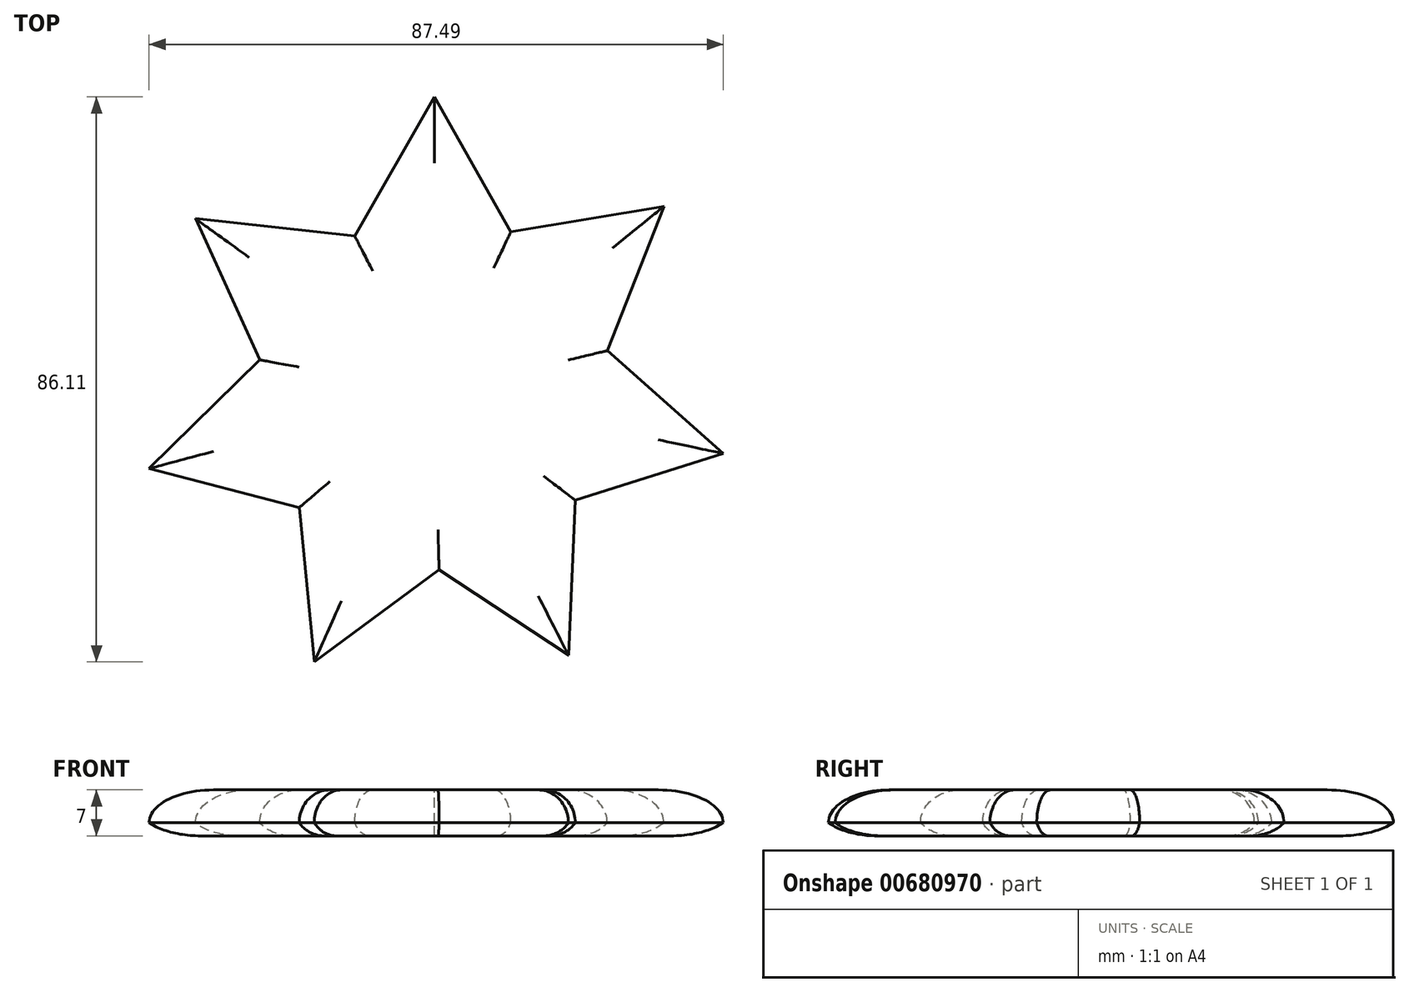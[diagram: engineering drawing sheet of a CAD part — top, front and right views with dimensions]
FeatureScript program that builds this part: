
annotation { "Feature Type Name" : "Feature", "Feature Type Description" : "" }
export const myFeature = defineFeature(function(context is Context, id is Id, definition is map)
    precondition{}
    {
        {
            var Q0;
            Q0=qCreatedBy(makeId("Top.planeOp"),FACE);
            var sketch = newSketch(context, id + "F0", { "sketchPlane" : qUnion([Q0])});
            skCircle(sketch, "E0", {"center": v(0, 0) * mm, "radius": 12.64 * mm});
            skCircle(sketch, "E1", {"center": v(0, 0) * mm, "radius": 17.03 * mm});
            skLineSegment(sketch, "E2", {"start": v(0, 0) * mm, "end": v(0, 45) * mm});
            skLineSegment(sketch, "E3", {"start": v(0, 0) * mm, "end": v(34.97, 28.32) * mm});
            skLineSegment(sketch, "E4", {"start": v(0, 0) * mm, "end": v(-18.3, -41.1) * mm});
            skLineSegment(sketch, "E5", {"start": v(0, 0) * mm, "end": v(-43.47, -11.65) * mm});
            skLineSegment(sketch, "E6", {"start": v(0, 0) * mm, "end": v(44.02, -9.36) * mm});
            skLineSegment(sketch, "E7", {"start": v(0, 0) * mm, "end": v(20.43, -40.1) * mm});
            skLineSegment(sketch, "E8", {"start": v(0, 0) * mm, "end": v(-36.4, 26.45) * mm});
            skLineSegment(sketch, "E9", {"start": v(0, 0) * mm, "end": v(-18.2, 13.23) * mm});
            skLineSegment(sketch, "E10", {"start": v(0, 0) * mm, "end": v(-21.73, -5.82) * mm});
            skLineSegment(sketch, "E11", {"start": v(0, 0) * mm, "end": v(-9.15, -20.55) * mm});
            skLineSegment(sketch, "E12", {"start": v(0, 0) * mm, "end": v(10.21, -20.05) * mm});
            skLineSegment(sketch, "E13", {"start": v(0, 0) * mm, "end": v(22, -4.68) * mm});
            skLineSegment(sketch, "E14", {"start": v(0, 0) * mm, "end": v(17.49, 14.16) * mm});
            skLineSegment(sketch, "E15", {"start": v(0, 0) * mm, "end": v(0, 22.5) * mm});
            skLineSegment(sketch, "E16", {"start": v(0, 22.5) * mm, "end": v(-18.2, 13.23) * mm});
            skLineSegment(sketch, "E17", {"start": v(-18.2, 13.23) * mm, "end": v(-21.73, -5.82) * mm});
            skLineSegment(sketch, "E18", {"start": v(-21.73, -5.82) * mm, "end": v(-9.15, -20.55) * mm});
            skLineSegment(sketch, "E19", {"start": v(-9.15, -20.55) * mm, "end": v(10.21, -20.05) * mm});
            skLineSegment(sketch, "E20", {"start": v(10.21, -20.05) * mm, "end": v(22, -4.68) * mm});
            skLineSegment(sketch, "E21", {"start": v(22, -4.68) * mm, "end": v(17.49, 14.16) * mm});
            skLineSegment(sketch, "E22", {"start": v(17.49, 14.16) * mm, "end": v(0, 22.5) * mm});
            skLineSegment(sketch, "E23", {"start": v(0, 45) * mm, "end": v(17.49, 14.16) * mm});
            skLineSegment(sketch, "E24", {"start": v(34.97, 28.32) * mm, "end": v(0, 22.5) * mm});
            skLineSegment(sketch, "E25", {"start": v(34.97, 28.32) * mm, "end": v(22, -4.68) * mm});
            skLineSegment(sketch, "E26", {"start": v(44.02, -9.36) * mm, "end": v(17.49, 14.16) * mm});
            skLineSegment(sketch, "E27", {"start": v(44.02, -9.36) * mm, "end": v(10.21, -20.05) * mm});
            skLineSegment(sketch, "E28", {"start": v(20.43, -40.1) * mm, "end": v(22, -4.68) * mm});
            skLineSegment(sketch, "E29", {"start": v(20.43, -40.1) * mm, "end": v(-9.15, -20.55) * mm});
            skLineSegment(sketch, "E30", {"start": v(-18.3, -41.1) * mm, "end": v(10.21, -20.05) * mm});
            skLineSegment(sketch, "E31", {"start": v(-18.3, -41.1) * mm, "end": v(-21.73, -5.82) * mm});
            skLineSegment(sketch, "E32", {"start": v(-43.47, -11.65) * mm, "end": v(-9.15, -20.55) * mm});
            skLineSegment(sketch, "E33", {"start": v(-43.47, -11.65) * mm, "end": v(-18.2, 13.23) * mm});
            skLineSegment(sketch, "E34", {"start": v(-36.4, 26.45) * mm, "end": v(-21.73, -5.82) * mm});
            skLineSegment(sketch, "E35", {"start": v(-36.4, 26.45) * mm, "end": v(0, 22.5) * mm});
            skLineSegment(sketch, "E36", {"start": v(0, 45) * mm, "end": v(-18.2, 13.23) * mm});
            skSolve(sketch);
        }
        {
            var Q0;
            {var subQ0=sQuery(id+"F0.wireOp",EDGE,"E7");Q0=makeQuery(id+"F0.imprint","IMPRINT",FACE,{"disambiguationData":[TD([[makeQuery(id+"F0.imprint","IMPRINT",EDGE,{"derivedFrom":subQ0}),-1.0]])]});}
            var Q1;
            {var subQ0=sQuery(id+"F0.wireOp",EDGE,"E4");Q1=makeQuery(id+"F0.imprint","IMPRINT",FACE,{"disambiguationData":[TD([[makeQuery(id+"F0.imprint","IMPRINT",EDGE,{"derivedFrom":subQ0}),-1.0]])]});}
            var Q2;
            {var subQ0=sQuery(id+"F0.wireOp",EDGE,"E5");Q2=makeQuery(id+"F0.imprint","IMPRINT",FACE,{"disambiguationData":[TD([[makeQuery(id+"F0.imprint","IMPRINT",EDGE,{"derivedFrom":subQ0}),1.0]])]});}
            var Q3;
            {var subQ0=sQuery(id+"F0.wireOp",EDGE,"E2");Q3=makeQuery(id+"F0.imprint","IMPRINT",FACE,{"disambiguationData":[TD([[makeQuery(id+"F0.imprint","IMPRINT",EDGE,{"derivedFrom":subQ0}),1.0]])]});}
            var Q4;
            {var subQ0=sQuery(id+"F0.wireOp",EDGE,"E5");Q4=makeQuery(id+"F0.imprint","IMPRINT",FACE,{"disambiguationData":[TD([[makeQuery(id+"F0.imprint","IMPRINT",EDGE,{"derivedFrom":subQ0}),-1.0]])]});}
            var Q5;
            {var subQ0=sQuery(id+"F0.wireOp",EDGE,"E7");Q5=makeQuery(id+"F0.imprint","IMPRINT",FACE,{"disambiguationData":[TD([[makeQuery(id+"F0.imprint","IMPRINT",EDGE,{"derivedFrom":subQ0}),1.0]])]});}
            var Q6;
            {var subQ0=sQuery(id+"F0.wireOp",EDGE,"E8");Q6=makeQuery(id+"F0.imprint","IMPRINT",FACE,{"disambiguationData":[TD([[makeQuery(id+"F0.imprint","IMPRINT",EDGE,{"derivedFrom":subQ0}),1.0]])]});}
            var Q7;
            {var subQ5=sQuery(id+"F0.wireOp",EDGE,"E19");Q7=makeQuery(id+"F0.imprint","IMPRINT",FACE,{"disambiguationData":[TD([[makeQuery(id+"F0.imprint","IMPRINT",EDGE,{"derivedFrom":subQ5}),1.0]])]});}
            var Q8;
            {var subQ0=sQuery(id+"F0.wireOp",EDGE,"E2");Q8=makeQuery(id+"F0.imprint","IMPRINT",FACE,{"disambiguationData":[TD([[makeQuery(id+"F0.imprint","IMPRINT",EDGE,{"derivedFrom":subQ0}),-1.0]])]});}
            var Q9;
            {var subQ0=sQuery(id+"F0.wireOp",EDGE,"E4");Q9=makeQuery(id+"F0.imprint","IMPRINT",FACE,{"disambiguationData":[TD([[makeQuery(id+"F0.imprint","IMPRINT",EDGE,{"derivedFrom":subQ0}),1.0]])]});}
            var Q10;
            {var subQ0=sQuery(id+"F0.wireOp",EDGE,"E16");Q10=makeQuery(id+"F0.imprint","IMPRINT",FACE,{"disambiguationData":[TD([[makeQuery(id+"F0.imprint","IMPRINT",EDGE,{"derivedFrom":subQ0}),-1.0]])]});}
            var Q11;
            {var subQ0=sQuery(id+"F0.wireOp",EDGE,"E11");var subQ1=sQuery(id+"F0.wireOp",EDGE,"E0");var subQ2=makeQuery(id+"F0.imprint","INTERSECT",VERTEX,{"derivedFrom":[subQ1,subQ0]});Q11=makeQuery(id+"F0.imprint","IMPRINT",FACE,{"disambiguationData":[TD([[makeQuery(id+"F0.imprint","IMPRINT",EDGE,{"disambiguationData":[TD([[subQ2,-1.0]])],"derivedFrom":subQ1}),-1.0]])]});}
            var Q12;
            {var subQ0=sQuery(id+"F0.wireOp",EDGE,"E3");Q12=makeQuery(id+"F0.imprint","IMPRINT",FACE,{"disambiguationData":[TD([[makeQuery(id+"F0.imprint","IMPRINT",EDGE,{"derivedFrom":subQ0}),-1.0]])]});}
            var Q13;
            {var subQ0=sQuery(id+"F0.wireOp",EDGE,"E3");Q13=makeQuery(id+"F0.imprint","IMPRINT",FACE,{"disambiguationData":[TD([[makeQuery(id+"F0.imprint","IMPRINT",EDGE,{"derivedFrom":subQ0}),1.0]])]});}
            var Q14;
            {var subQ0=sQuery(id+"F0.wireOp",EDGE,"E22");Q14=makeQuery(id+"F0.imprint","IMPRINT",FACE,{"disambiguationData":[TD([[makeQuery(id+"F0.imprint","IMPRINT",EDGE,{"derivedFrom":subQ0}),-1.0]])]});}
            var Q15;
            {var subQ0=sQuery(id+"F0.wireOp",EDGE,"E12");var subQ1=sQuery(id+"F0.wireOp",EDGE,"E0");var subQ2=makeQuery(id+"F0.imprint","INTERSECT",VERTEX,{"derivedFrom":[subQ1,subQ0]});Q15=makeQuery(id+"F0.imprint","IMPRINT",FACE,{"disambiguationData":[TD([[makeQuery(id+"F0.imprint","IMPRINT",EDGE,{"disambiguationData":[TD([[subQ2,-1.0]])],"derivedFrom":subQ1}),-1.0]])]});}
            var Q16;
            {var subQ0=sQuery(id+"F0.wireOp",EDGE,"E6");Q16=makeQuery(id+"F0.imprint","IMPRINT",FACE,{"disambiguationData":[TD([[makeQuery(id+"F0.imprint","IMPRINT",EDGE,{"derivedFrom":subQ0}),-1.0]])]});}
            var Q17;
            {var subQ0=sQuery(id+"F0.wireOp",EDGE,"E18");Q17=makeQuery(id+"F0.imprint","IMPRINT",FACE,{"disambiguationData":[TD([[makeQuery(id+"F0.imprint","IMPRINT",EDGE,{"derivedFrom":subQ0}),-1.0]])]});}
            var Q18;
            {var subQ0=sQuery(id+"F0.wireOp",EDGE,"E6");Q18=makeQuery(id+"F0.imprint","IMPRINT",FACE,{"disambiguationData":[TD([[makeQuery(id+"F0.imprint","IMPRINT",EDGE,{"derivedFrom":subQ0}),1.0]])]});}
            var Q19;
            {var subQ0=sQuery(id+"F0.wireOp",EDGE,"E9");var subQ1=sQuery(id+"F0.wireOp",EDGE,"E0");var subQ2=makeQuery(id+"F0.imprint","INTERSECT",VERTEX,{"derivedFrom":[subQ1,subQ0]});Q19=makeQuery(id+"F0.imprint","IMPRINT",FACE,{"disambiguationData":[TD([[makeQuery(id+"F0.imprint","IMPRINT",EDGE,{"disambiguationData":[TD([[subQ2,-1.0]])],"derivedFrom":subQ1}),-1.0]])]});}
            var Q20;
            {var subQ5=sQuery(id+"F0.wireOp",EDGE,"E17");Q20=makeQuery(id+"F0.imprint","IMPRINT",FACE,{"disambiguationData":[TD([[makeQuery(id+"F0.imprint","IMPRINT",EDGE,{"derivedFrom":subQ5}),1.0]])]});}
            var Q21;
            {var subQ0=sQuery(id+"F0.wireOp",EDGE,"E19");Q21=makeQuery(id+"F0.imprint","IMPRINT",FACE,{"disambiguationData":[TD([[makeQuery(id+"F0.imprint","IMPRINT",EDGE,{"derivedFrom":subQ0}),-1.0]])]});}
            var Q22;
            {var subQ0=sQuery(id+"F0.wireOp",EDGE,"E15");var subQ1=sQuery(id+"F0.wireOp",EDGE,"E0");var subQ2=makeQuery(id+"F0.imprint","INTERSECT",VERTEX,{"derivedFrom":[subQ1,subQ0]});Q22=makeQuery(id+"F0.imprint","IMPRINT",FACE,{"disambiguationData":[TD([[makeQuery(id+"F0.imprint","IMPRINT",EDGE,{"disambiguationData":[TD([[subQ2,1.0]])],"derivedFrom":subQ1}),-1.0]])]});}
            var Q23;
            {var subQ0=sQuery(id+"F0.wireOp",EDGE,"E8");Q23=makeQuery(id+"F0.imprint","IMPRINT",FACE,{"disambiguationData":[TD([[makeQuery(id+"F0.imprint","IMPRINT",EDGE,{"derivedFrom":subQ0}),-1.0]])]});}
            var Q24;
            {var subQ5=sQuery(id+"F0.wireOp",EDGE,"E20");Q24=makeQuery(id+"F0.imprint","IMPRINT",FACE,{"disambiguationData":[TD([[makeQuery(id+"F0.imprint","IMPRINT",EDGE,{"derivedFrom":subQ5}),1.0]])]});}
            var Q25;
            {var subQ0=sQuery(id+"F0.wireOp",EDGE,"E15");var subQ1=sQuery(id+"F0.wireOp",EDGE,"E0");var subQ2=makeQuery(id+"F0.imprint","INTERSECT",VERTEX,{"derivedFrom":[subQ1,subQ0]});Q25=makeQuery(id+"F0.imprint","IMPRINT",FACE,{"disambiguationData":[TD([[makeQuery(id+"F0.imprint","IMPRINT",EDGE,{"disambiguationData":[TD([[subQ2,-1.0]])],"derivedFrom":subQ1}),-1.0]])]});}
            var Q26;
            {var subQ5=sQuery(id+"F0.wireOp",EDGE,"E16");Q26=makeQuery(id+"F0.imprint","IMPRINT",FACE,{"disambiguationData":[TD([[makeQuery(id+"F0.imprint","IMPRINT",EDGE,{"derivedFrom":subQ5}),1.0]])]});}
            var Q27;
            {var subQ0=sQuery(id+"F0.wireOp",EDGE,"E14");var subQ1=sQuery(id+"F0.wireOp",EDGE,"E0");var subQ2=makeQuery(id+"F0.imprint","INTERSECT",VERTEX,{"derivedFrom":[subQ1,subQ0]});Q27=makeQuery(id+"F0.imprint","IMPRINT",FACE,{"disambiguationData":[TD([[makeQuery(id+"F0.imprint","IMPRINT",EDGE,{"disambiguationData":[TD([[subQ2,1.0]])],"derivedFrom":subQ1}),-1.0]])]});}
            var Q28;
            {var subQ5=sQuery(id+"F0.wireOp",EDGE,"E18");Q28=makeQuery(id+"F0.imprint","IMPRINT",FACE,{"disambiguationData":[TD([[makeQuery(id+"F0.imprint","IMPRINT",EDGE,{"derivedFrom":subQ5}),1.0]])]});}
            var Q29;
            {var subQ0=sQuery(id+"F0.wireOp",EDGE,"E17");Q29=makeQuery(id+"F0.imprint","IMPRINT",FACE,{"disambiguationData":[TD([[makeQuery(id+"F0.imprint","IMPRINT",EDGE,{"derivedFrom":subQ0}),-1.0]])]});}
            var Q30;
            {var subQ0=sQuery(id+"F0.wireOp",EDGE,"E10");var subQ1=sQuery(id+"F0.wireOp",EDGE,"E0");var subQ2=makeQuery(id+"F0.imprint","INTERSECT",VERTEX,{"derivedFrom":[subQ1,subQ0]});Q30=makeQuery(id+"F0.imprint","IMPRINT",FACE,{"disambiguationData":[TD([[makeQuery(id+"F0.imprint","IMPRINT",EDGE,{"disambiguationData":[TD([[subQ2,-1.0]])],"derivedFrom":subQ1}),-1.0]])]});}
            var Q31;
            {var subQ5=sQuery(id+"F0.wireOp",EDGE,"E21");Q31=makeQuery(id+"F0.imprint","IMPRINT",FACE,{"disambiguationData":[TD([[makeQuery(id+"F0.imprint","IMPRINT",EDGE,{"derivedFrom":subQ5}),1.0]])]});}
            var Q32;
            {var subQ0=sQuery(id+"F0.wireOp",EDGE,"E20");Q32=makeQuery(id+"F0.imprint","IMPRINT",FACE,{"disambiguationData":[TD([[makeQuery(id+"F0.imprint","IMPRINT",EDGE,{"derivedFrom":subQ0}),-1.0]])]});}
            var Q33;
            {var subQ0=sQuery(id+"F0.wireOp",EDGE,"E21");Q33=makeQuery(id+"F0.imprint","IMPRINT",FACE,{"disambiguationData":[TD([[makeQuery(id+"F0.imprint","IMPRINT",EDGE,{"derivedFrom":subQ0}),-1.0]])]});}
            var Q34;
            {var subQ5=sQuery(id+"F0.wireOp",EDGE,"E22");Q34=makeQuery(id+"F0.imprint","IMPRINT",FACE,{"disambiguationData":[TD([[makeQuery(id+"F0.imprint","IMPRINT",EDGE,{"derivedFrom":subQ5}),1.0]])]});}
            extrude(context, id + "F1", {"entities" : qUnion([Q0, Q1, Q2, Q3, Q4, Q5, Q6, Q7, Q8, Q9, Q10, Q11, Q12, Q13, Q14, Q15, Q16, Q17, Q18, Q19, Q20, Q21, Q22, Q23, Q24, Q25, Q26, Q27, Q28, Q29, Q30, Q31, Q32, Q33, Q34]), "depth" : 7 * mm, "offsetDistance" : 25 * mm});
        }
        {
            var Q0;
            Q0=makeQuery(id+"F1.opExtrude","CAP_EDGE",EDGE,{"disambiguationData":[OSD([sQuery(id+"F0.wireOp",EDGE,"E35")])],"isStart":false});
            var Q1;
            Q1=makeQuery(id+"F1.opExtrude","CAP_EDGE",EDGE,{"disambiguationData":[OSD([sQuery(id+"F0.wireOp",EDGE,"E36")])],"isStart":false});
            var Q2;
            Q2=makeQuery(id+"F1.opExtrude","CAP_EDGE",EDGE,{"disambiguationData":[OSD([sQuery(id+"F0.wireOp",EDGE,"E23")])],"isStart":false});
            var Q3;
            Q3=makeQuery(id+"F1.opExtrude","CAP_EDGE",EDGE,{"disambiguationData":[OSD([sQuery(id+"F0.wireOp",EDGE,"E24")])],"isStart":false});
            var Q4;
            Q4=makeQuery(id+"F1.opExtrude","CAP_EDGE",EDGE,{"disambiguationData":[OSD([sQuery(id+"F0.wireOp",EDGE,"E26")])],"isStart":false});
            var Q5;
            Q5=makeQuery(id+"F1.opExtrude","CAP_EDGE",EDGE,{"disambiguationData":[OSD([sQuery(id+"F0.wireOp",EDGE,"E27")])],"isStart":false});
            var Q6;
            Q6=makeQuery(id+"F1.opExtrude","CAP_EDGE",EDGE,{"disambiguationData":[OSD([sQuery(id+"F0.wireOp",EDGE,"E28")])],"isStart":false});
            var Q7;
            Q7=makeQuery(id+"F1.opExtrude","CAP_EDGE",EDGE,{"disambiguationData":[OSD([sQuery(id+"F0.wireOp",EDGE,"E29")])],"isStart":false});
            var Q8;
            Q8=makeQuery(id+"F1.opExtrude","CAP_EDGE",EDGE,{"disambiguationData":[OSD([sQuery(id+"F0.wireOp",EDGE,"E30")])],"isStart":false});
            var Q9;
            Q9=makeQuery(id+"F1.opExtrude","CAP_EDGE",EDGE,{"disambiguationData":[OSD([sQuery(id+"F0.wireOp",EDGE,"E31")])],"isStart":false});
            var Q10;
            Q10=makeQuery(id+"F1.opExtrude","CAP_EDGE",EDGE,{"disambiguationData":[OSD([sQuery(id+"F0.wireOp",EDGE,"E32")])],"isStart":false});
            var Q11;
            Q11=makeQuery(id+"F1.opExtrude","CAP_EDGE",EDGE,{"disambiguationData":[OSD([sQuery(id+"F0.wireOp",EDGE,"E33")])],"isStart":false});
            var Q12;
            Q12=makeQuery(id+"F1.opExtrude","CAP_EDGE",EDGE,{"disambiguationData":[OSD([sQuery(id+"F0.wireOp",EDGE,"E34")])],"isStart":false});
            var Q13;
            Q13=makeQuery(id+"F1.opExtrude","CAP_EDGE",EDGE,{"disambiguationData":[OSD([sQuery(id+"F0.wireOp",EDGE,"E25")])],"isStart":false});
            fillet(context, id + "F2", {"entities" : qUnion([Q0, Q1, Q2, Q3, Q4, Q5, Q6, Q7, Q8, Q9, Q10, Q11, Q12, Q13]), "radius" : 5 * mm, "tangentPropagation" : true, "allowEdgeOverflow" : false});
        }
        {
            var Q0;
            Q0=makeQuery(id+"F1.opExtrude","CAP_EDGE",EDGE,{"disambiguationData":[OSD([sQuery(id+"F0.wireOp",EDGE,"E24")])],"isStart":true});
            var Q1;
            Q1=makeQuery(id+"F1.opExtrude","CAP_EDGE",EDGE,{"disambiguationData":[OSD([sQuery(id+"F0.wireOp",EDGE,"E23")])],"isStart":true});
            var Q2;
            Q2=makeQuery(id+"F1.opExtrude","CAP_EDGE",EDGE,{"disambiguationData":[OSD([sQuery(id+"F0.wireOp",EDGE,"E36")])],"isStart":true});
            var Q3;
            Q3=makeQuery(id+"F1.opExtrude","CAP_EDGE",EDGE,{"disambiguationData":[OSD([sQuery(id+"F0.wireOp",EDGE,"E35")])],"isStart":true});
            var Q4;
            Q4=makeQuery(id+"F1.opExtrude","CAP_EDGE",EDGE,{"disambiguationData":[OSD([sQuery(id+"F0.wireOp",EDGE,"E34")])],"isStart":true});
            var Q5;
            Q5=makeQuery(id+"F1.opExtrude","CAP_EDGE",EDGE,{"disambiguationData":[OSD([sQuery(id+"F0.wireOp",EDGE,"E33")])],"isStart":true});
            var Q6;
            Q6=makeQuery(id+"F1.opExtrude","CAP_EDGE",EDGE,{"disambiguationData":[OSD([sQuery(id+"F0.wireOp",EDGE,"E32")])],"isStart":true});
            var Q7;
            Q7=makeQuery(id+"F1.opExtrude","CAP_EDGE",EDGE,{"disambiguationData":[OSD([sQuery(id+"F0.wireOp",EDGE,"E31")])],"isStart":true});
            var Q8;
            Q8=makeQuery(id+"F1.opExtrude","CAP_EDGE",EDGE,{"disambiguationData":[OSD([sQuery(id+"F0.wireOp",EDGE,"E30")])],"isStart":true});
            var Q9;
            Q9=makeQuery(id+"F1.opExtrude","CAP_EDGE",EDGE,{"disambiguationData":[OSD([sQuery(id+"F0.wireOp",EDGE,"E29")])],"isStart":true});
            var Q10;
            Q10=makeQuery(id+"F1.opExtrude","CAP_EDGE",EDGE,{"disambiguationData":[OSD([sQuery(id+"F0.wireOp",EDGE,"E27")])],"isStart":true});
            var Q11;
            Q11=makeQuery(id+"F1.opExtrude","CAP_EDGE",EDGE,{"disambiguationData":[OSD([sQuery(id+"F0.wireOp",EDGE,"E26")])],"isStart":true});
            var Q12;
            Q12=makeQuery(id+"F1.opExtrude","CAP_EDGE",EDGE,{"disambiguationData":[OSD([sQuery(id+"F0.wireOp",EDGE,"E25")])],"isStart":true});
            var Q13;
            Q13=makeQuery(id+"F1.opExtrude","CAP_EDGE",EDGE,{"disambiguationData":[OSD([sQuery(id+"F0.wireOp",EDGE,"E28")])],"isStart":true});
            fillet(context, id + "F3", {"entities" : qUnion([Q0, Q1, Q2, Q3, Q4, Q5, Q6, Q7, Q8, Q9, Q10, Q11, Q12, Q13]), "radius" : 5 * mm, "tangentPropagation" : true, "allowEdgeOverflow" : false});
        }
    });
